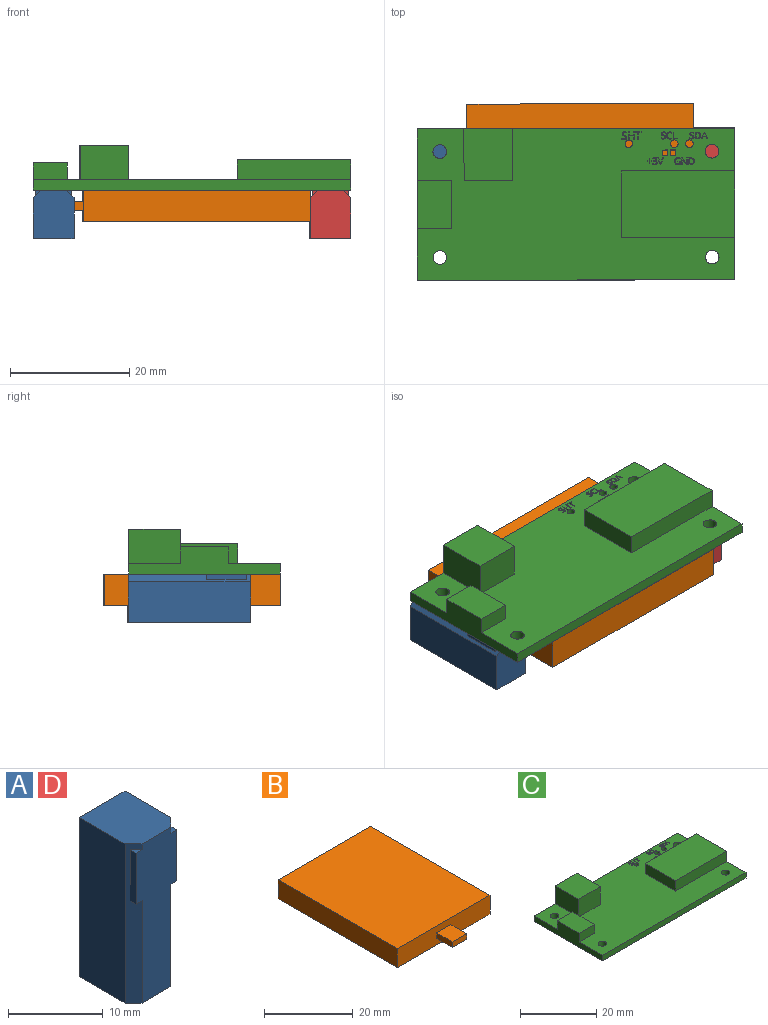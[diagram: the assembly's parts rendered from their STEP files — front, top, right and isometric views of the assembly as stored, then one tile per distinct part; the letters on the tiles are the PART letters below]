
ASSEMBLY  parts=4 mates=4
PART A: 14 faces, bbox 6.9x8.1x20.6 mm
  f0: plane 20.57x6.86mm, normal (-1,0,0), area 141.1mm2, adj f2,f3,f4,f7
  f1: plane 20.57x6.86mm, normal (1,0,0), area 141.1mm2, adj f2,f3,f4,f6
  f2: plane 20.57x6.86mm, normal (0,1,0), area 141.1mm2, adj f0,f1,f3,f4
  f3: plane 8.13x6.86mm, normal (0,0,1), area 54.1mm2, adj f0,f1,f2,f5,f6,f7
  f4: plane 8.13x6.86mm, normal (0,0,-1), area 54.1mm2, adj f0,f1,f2,f5,f6,f7
  f5: plane 20.57x6.1mm, normal (0,-1,0), area 100.6mm2, adj f3,f4,f6,f7,f8,f9,f10,f11
  f6: plane 20.57x1.27mm, normal (0.71,-0.71,0), area 28.6mm2, adj f1,f3,f4,f5,f11,f12,f13
  f7: plane 20.57x1.27mm, normal (-0.71,-0.71,0), area 28.6mm2, adj f0,f3,f4,f5,f8,f9,f10
  f8: plane 6.6x0.89mm, normal (-1,0,0), area 5.9mm2, adj f5,f7,f9,f10
  f9: plane 0.89x0.89mm, normal (0,0,-1), area 0.4mm2, adj f5,f7,f8
  f10: plane 0.89x0.89mm, normal (0,0,1), area 0.4mm2, adj f5,f7,f8
  f11: plane 0.89x0.89mm, normal (0,0,-1), area 0.4mm2, adj f5,f6,f12
  f12: plane 6.6x0.89mm, normal (1,0,0), area 5.9mm2, adj f5,f6,f11,f13
  f13: plane 0.89x0.89mm, normal (0,0,1), area 0.4mm2, adj f5,f6,f12
PART B: 11 faces, bbox 29.6x43.2x5.2 mm
  f0: plane 29.57x5.23mm, normal (0,-1,0), area 147.7mm2, adj f1,f2,f4,f5,f6,f7,f8,f9
  f1: plane 38.1x5.23mm, normal (-1,0,0), area 199.4mm2, adj f0,f3,f4,f5
  f2: plane 38.1x5.23mm, normal (1,0,0), area 199.4mm2, adj f0,f3,f4,f5
  f3: plane 29.57x5.23mm, normal (0,1,0), area 154.7mm2, adj f1,f2,f4,f5
  f4: plane 38.1x29.57mm, normal (0,0,1), area 1126.4mm2, adj f0,f1,f2,f3
  f5: plane 38.1x29.57mm, normal (0,0,-1), area 1126.4mm2, adj f0,f1,f2,f3
  f6: plane 5.08x1.52mm, normal (-1,0,0), area 7.7mm2, adj f0,f7,f9,f10
  f7: plane 5.08x4.57mm, normal (0,0,-1), area 23.2mm2, adj f0,f6,f8,f10
  f8: plane 5.08x1.52mm, normal (1,0,0), area 7.7mm2, adj f0,f7,f9,f10
  f9: plane 5.08x4.57mm, normal (0,0,1), area 23.2mm2, adj f0,f6,f8,f10
  f10: plane 4.57x1.52mm, normal (0,-1,0), area 7mm2, adj f6,f7,f8,f9
PART C: 292 faces, bbox 53.3x25.4x7.5 mm
  f0: plane 53.34x25.4mm, normal (0,0,1), area 997.2mm2, adj f1,f2,f3,f4,f5,f6,f7,f8
  f1: plane 25.4x4.57mm, normal (-1,0,0), area 67.9mm2, adj f0,f2,f19,f20,f29,f31,f32
  f2: plane 53.34x1.78mm, normal (0,-1,0), area 94.8mm2, adj f0,f1,f3,f20
  f3: plane 25.4x5.08mm, normal (1,0,0), area 82.1mm2, adj f0,f2,f19,f20,f21,f22,f24
  f4: plane 1.78x0.95mm, normal (0,-1,0), area 1.7mm2, adj f0,f5,f10,f20
  f5: plane 1.78x0.96mm, normal (-1,0,0), area 1.7mm2, adj f0,f4,f6,f20
  f6: plane 1.78x0.95mm, normal (0,1,0), area 1.7mm2, adj f0,f5,f10,f20
  f7: plane 1.78x0.88mm, normal (0,-1,0), area 1.6mm2, adj f0,f8,f11,f20
  f8: plane 1.78x0.98mm, normal (-1,0,0), area 1.7mm2, adj f0,f7,f9,f20
  f9: plane 1.78x0.88mm, normal (0,1,0), area 1.6mm2, adj f0,f8,f11,f20
  f10: plane 1.78x0.96mm, normal (1,0,0), area 1.7mm2, adj f0,f4,f6,f20
  f11: plane 1.78x0.98mm, normal (1,0,0), area 1.7mm2, adj f0,f7,f9,f20
  f12: cylinder r=1.14mm len=2.29mm, axis (0,0,-1), area 12.8mm2, adj f0,f20
  f13: cylinder r=1.14mm len=2.29mm, axis (0,0,-1), area 12.8mm2, adj f0,f20
  f14: cylinder r=1.14mm len=2.29mm, axis (0,0,-1), area 12.8mm2, adj f0,f20
  f15: cylinder r=1.14mm len=2.29mm, axis (0,0,-1), area 12.8mm2, adj f0,f20
  f16: cylinder r=0.64mm len=1.78mm, axis (0,0,-1), area 7.1mm2, adj f0,f20
  f17: cylinder r=0.64mm len=1.78mm, axis (0,0,-1), area 7.1mm2, adj f0,f20
  f18: cylinder r=0.64mm len=1.78mm, axis (0,0,-1), area 7.1mm2, adj f0,f20
  f19: plane 53.34x7.49mm, normal (0,1,0), area 141.3mm2, adj f0,f1,f3,f20,f25,f26,f28
  f20: plane 53.34x25.4mm, normal (0,0,-1), area 1332.9mm2, adj f1,f2,f3,f4,f5,f6,f7,f8
  f21: plane 19.05x3.3mm, normal (0,-1,0), area 62.9mm2, adj f0,f3,f23,f24
  f22: plane 19.05x3.3mm, normal (0,1,0), area 62.9mm2, adj f0,f3,f23,f24
  f23: plane 11.18x3.3mm, normal (-1,0,0), area 36.9mm2, adj f0,f21,f22,f24
  f24: plane 19.05x11.18mm, normal (0,0,1), area 212.9mm2, adj f3,f21,f22,f23
  f25: plane 8.64x5.72mm, normal (1,0,0), area 49.4mm2, adj f0,f19,f27,f28
  f26: plane 8.64x5.72mm, normal (-1,0,0), area 49.4mm2, adj f0,f19,f27,f28
  f27: plane 8.13x5.72mm, normal (0,-1,0), area 46.5mm2, adj f0,f25,f26,f28
  f28: plane 8.64x8.13mm, normal (0,0,1), area 70.2mm2, adj f19,f25,f26,f27
  f29: plane 5.72x2.79mm, normal (0,-1,0), area 16mm2, adj f0,f1,f30,f32
  f30: plane 8.13x2.79mm, normal (1,0,0), area 22.7mm2, adj f0,f29,f31,f32
  f31: plane 5.72x2.79mm, normal (0,1,0), area 16mm2, adj f0,f1,f30,f32
  f32: plane 8.13x5.72mm, normal (0,0,1), area 46.5mm2, adj f1,f29,f30,f31
  f33: extruded ~0.19x0.13mm, area 0mm2, adj f0,f34,f57,f58
  f34: extruded ~0.25x0.14mm, area 0mm2, adj f0,f33,f35,f58
  f35: extruded ~0.16x0.13mm, area 0mm2, adj f0,f34,f36,f58
  f36: extruded ~0.13x0.07mm, area 0mm2, adj f0,f35,f37,f58
  f37: extruded ~0.13x0.1mm, area 0mm2, adj f0,f36,f38,f58
  f38: extruded ~0.13x0.13mm, area 0mm2, adj f0,f37,f39,f58
  f39: extruded ~0.17x0.13mm, area 0mm2, adj f0,f38,f40,f58
  f40: extruded ~0.28x0.13mm, area 0mm2, adj f0,f39,f41,f58
  f41: plane 0.13x0.12mm, normal (-0.94,0.34,0), area 0mm2, adj f0,f40,f42,f58
  f42: extruded ~0.31x0.13mm, area 0mm2, adj f0,f41,f43,f58
  f43: extruded ~0.26x0.13mm, area 0mm2, adj f0,f42,f44,f58
  f44: extruded ~0.21x0.13mm, area 0mm2, adj f0,f43,f45,f58
  f45: extruded ~0.2x0.13mm, area 0mm2, adj f0,f44,f46,f58
  f46: extruded ~0.23x0.14mm, area 0mm2, adj f0,f45,f47,f58
  f47: extruded ~0.17x0.13mm, area 0mm2, adj f0,f46,f48,f58
  f48: extruded ~0.13x0.08mm, area 0mm2, adj f0,f47,f49,f58
  f49: extruded ~0.13x0.1mm, area 0mm2, adj f0,f48,f50,f58
  f50: extruded ~0.14x0.13mm, area 0mm2, adj f0,f49,f51,f58
  f51: extruded ~0.2x0.13mm, area 0mm2, adj f0,f50,f52,f58
  f52: extruded ~0.16x0.13mm, area 0mm2, adj f0,f51,f53,f58
  f53: extruded ~0.15x0.13mm, area 0mm2, adj f0,f52,f54,f58
  f54: plane 0.13x0.13mm, normal (1,0,0), area 0mm2, adj f0,f53,f55,f58
  f55: extruded ~0.31x0.13mm, area 0mm2, adj f0,f54,f56,f58
  f56: extruded ~0.3x0.13mm, area 0mm2, adj f0,f55,f57,f58
  f57: extruded ~0.24x0.13mm, area 0mm2, adj f0,f33,f56,f58
  f58: plane 1.18x0.72mm, normal (0,0,1), area 0.3mm2, adj f33,f34,f35,f36,f37,f38,f39,f40
  f59: extruded ~0.22x0.13mm, area 0mm2, adj f0,f60,f83,f84
  f60: extruded ~0.28x0.16mm, area 0mm2, adj f0,f59,f61,f84
  f61: extruded ~0.18x0.13mm, area 0mm2, adj f0,f60,f62,f84
  f62: extruded ~0.13x0.08mm, area 0mm2, adj f0,f61,f63,f84
  f63: extruded ~0.13x0.11mm, area 0mm2, adj f0,f62,f64,f84
  f64: extruded ~0.14x0.13mm, area 0mm2, adj f0,f63,f65,f84
  f65: extruded ~0.19x0.13mm, area 0mm2, adj f0,f64,f66,f84
  f66: extruded ~0.31x0.13mm, area 0mm2, adj f0,f65,f67,f84
  f67: plane 0.13x0.13mm, normal (-0.94,0.34,0), area 0mm2, adj f0,f66,f68,f84
  f68: extruded ~0.36x0.13mm, area 0mm2, adj f0,f67,f69,f84
  f69: extruded ~0.3x0.13mm, area 0mm2, adj f0,f68,f70,f84
  f70: extruded ~0.24x0.13mm, area 0mm2, adj f0,f69,f71,f84
  f71: extruded ~0.23x0.13mm, area 0mm2, adj f0,f70,f72,f84
  f72: extruded ~0.26x0.15mm, area 0mm2, adj f0,f71,f73,f84
  f73: extruded ~0.19x0.13mm, area 0mm2, adj f0,f72,f74,f84
  f74: extruded ~0.13x0.09mm, area 0mm2, adj f0,f73,f75,f84
  f75: extruded ~0.13x0.11mm, area 0mm2, adj f0,f74,f76,f84
  f76: extruded ~0.16x0.13mm, area 0mm2, adj f0,f75,f77,f84
  f77: extruded ~0.23x0.13mm, area 0mm2, adj f0,f76,f78,f84
  f78: extruded ~0.19x0.13mm, area 0mm2, adj f0,f77,f79,f84
  f79: extruded ~0.17x0.13mm, area 0mm2, adj f0,f78,f80,f84
  f80: plane 0.15x0.13mm, normal (1,0,0), area 0mm2, adj f0,f79,f81,f84
  f81: extruded ~0.35x0.13mm, area 0mm2, adj f0,f80,f82,f84
  f82: extruded ~0.34x0.13mm, area 0mm2, adj f0,f81,f83,f84
  f83: extruded ~0.27x0.13mm, area 0mm2, adj f0,f59,f82,f84
  f84: plane 1.33x0.81mm, normal (0,0,1), area 0.4mm2, adj f59,f60,f61,f62,f63,f64,f65,f66
  f85: plane 1.29x0.13mm, normal (-1,0,0), area 0.2mm2, adj f0,f86,f96,f97
  f86: plane 0.15x0.13mm, normal (0,-1,0), area 0mm2, adj f0,f85,f87,f97
  f87: plane 0.55x0.13mm, normal (1,0,0), area 0.1mm2, adj f0,f86,f88,f97
  f88: plane 0.68x0.13mm, normal (0,-1,0), area 0.1mm2, adj f0,f87,f89,f97
  f89: plane 0.55x0.13mm, normal (-1,0,0), area 0.1mm2, adj f0,f88,f90,f97
  f90: plane 0.15x0.13mm, normal (0,-1,0), area 0mm2, adj f0,f89,f91,f97
  f91: plane 1.29x0.13mm, normal (1,0,0), area 0.2mm2, adj f0,f90,f92,f97
  f92: plane 0.15x0.13mm, normal (0,1,0), area 0mm2, adj f0,f91,f93,f97
  f93: plane 0.61x0.13mm, normal (-1,0,0), area 0.1mm2, adj f0,f92,f94,f97
  f94: plane 0.68x0.13mm, normal (0,1,0), area 0.1mm2, adj f0,f93,f95,f97
  f95: plane 0.61x0.13mm, normal (1,0,0), area 0.1mm2, adj f0,f94,f96,f97
  f96: plane 0.15x0.13mm, normal (0,1,0), area 0mm2, adj f0,f85,f95,f97
  f97: plane 1.29x0.98mm, normal (0,0,1), area 0.5mm2, adj f85,f86,f87,f88,f89,f90,f91,f92
  f98: plane 1.16x0.13mm, normal (-1,0,0), area 0.1mm2, adj f0,f99,f105,f106
  f99: plane 0.41x0.13mm, normal (0,1,0), area 0.1mm2, adj f0,f98,f100,f106
  f100: plane 0.13x0.13mm, normal (-1,0,0), area 0mm2, adj f0,f99,f101,f106
  f101: plane 0.97x0.13mm, normal (0,-1,0), area 0.1mm2, adj f0,f100,f102,f106
  f102: plane 0.13x0.13mm, normal (1,0,0), area 0mm2, adj f0,f101,f103,f106
  f103: plane 0.41x0.13mm, normal (0,1,0), area 0.1mm2, adj f0,f102,f104,f106
  f104: plane 1.16x0.13mm, normal (1,0,0), area 0.1mm2, adj f0,f103,f105,f106
  f105: plane 0.15x0.13mm, normal (0,1,0), area 0mm2, adj f0,f98,f104,f106
  f106: plane 1.29x0.97mm, normal (0,0,1), area 0.3mm2, adj f98,f99,f100,f101,f102,f103,f104,f105
  f107: extruded ~0.41x0.15mm, area 0.1mm2, adj f0,f108,f120,f121
  f108: extruded ~0.41x0.15mm, area 0.1mm2, adj f0,f107,f109,f121
  f109: plane 0.35x0.13mm, normal (0,-1,0), area 0mm2, adj f0,f108,f110,f121
  f110: plane 1.14x0.13mm, normal (1,0,0), area 0.1mm2, adj f0,f109,f111,f121
  f111: plane 0.32x0.13mm, normal (0,1,0), area 0mm2, adj f0,f110,f112,f121
  f112: extruded ~0.44x0.15mm, area 0.1mm2, adj f0,f111,f120,f121
  f113: extruded ~0.35x0.13mm, area 0mm2, adj f114,f119,f121,f122
  f114: extruded ~0.36x0.13mm, area 0mm2, adj f113,f115,f121,f122
  f115: plane 0.16x0.13mm, normal (0,-1,0), area 0mm2, adj f114,f116,f121,f122
  f116: plane 0.91x0.13mm, normal (-1,0,0), area 0.1mm2, adj f115,f117,f121,f122
  f117: plane 0.19x0.13mm, normal (0,1,0), area 0mm2, adj f116,f118,f121,f122
  f118: extruded ~0.33x0.13mm, area 0mm2, adj f117,f119,f121,f122
  f119: extruded ~0.34x0.13mm, area 0mm2, adj f113,f118,f121,f122
  f120: extruded ~0.43x0.15mm, area 0.1mm2, adj f0,f107,f112,f121
  f121: plane 1.14x0.91mm, normal (0,0,1), area 0.4mm2, adj f107,f108,f109,f110,f111,f112,f113,f114
  f122: plane 0.91x0.64mm, normal (0,0,1), area 0.5mm2, adj f113,f114,f115,f116,f117,f118,f119
  f123: plane 0.14x0.13mm, normal (0,1,0), area 0mm2, adj f0,f124,f135,f136
  f124: plane 1.15x0.45mm, normal (-0.93,-0.36,0), area 0.2mm2, adj f0,f123,f125,f136
  f125: plane 0.13x0.11mm, normal (0,-1,0), area 0mm2, adj f0,f124,f126,f136
  f126: plane 1.15x0.45mm, normal (0.93,-0.37,0), area 0.2mm2, adj f0,f125,f127,f136
  f127: plane 0.13x0.13mm, normal (0,1,0), area 0mm2, adj f0,f126,f128,f136
  f128: plane 0.36x0.14mm, normal (-0.93,0.36,0), area 0mm2, adj f0,f127,f129,f136
  f129: plane 0.46x0.13mm, normal (0,1,0), area 0.1mm2, adj f0,f128,f135,f136
  f130: plane 0.37x0.13mm, normal (0,-1,0), area 0mm2, adj f131,f134,f136,f137
  f131: plane 0.35x0.13mm, normal (-0.94,0.35,0), area 0mm2, adj f130,f132,f136,f137
  f132: extruded ~0.17x0.13mm, area 0mm2, adj f131,f133,f136,f137
  f133: extruded ~0.17x0.13mm, area 0mm2, adj f132,f134,f136,f137
  f134: plane 0.35x0.13mm, normal (0.94,0.35,0), area 0mm2, adj f130,f133,f136,f137
  f135: plane 0.36x0.14mm, normal (0.93,0.36,0), area 0mm2, adj f0,f123,f129,f136
  f136: plane 1.15x1.01mm, normal (0,0,1), area 0.3mm2, adj f123,f124,f125,f126,f127,f128,f129,f130
  f137: plane 0.52x0.37mm, normal (0,0,1), area 0.1mm2, adj f130,f131,f132,f133,f134
  f138: extruded ~0.41x0.15mm, area 0.1mm2, adj f0,f139,f151,f152
  f139: extruded ~0.41x0.15mm, area 0.1mm2, adj f0,f138,f140,f152
  f140: plane 0.34x0.13mm, normal (0,-1,0), area 0mm2, adj f0,f139,f141,f152
  f141: plane 1.12x0.13mm, normal (1,0,0), area 0.1mm2, adj f0,f140,f142,f152
  f142: plane 0.31x0.13mm, normal (0,1,0), area 0mm2, adj f0,f141,f143,f152
  f143: extruded ~0.43x0.15mm, area 0.1mm2, adj f0,f142,f151,f152
  f144: extruded ~0.34x0.13mm, area 0mm2, adj f145,f150,f152,f153
  f145: extruded ~0.35x0.13mm, area 0mm2, adj f144,f146,f152,f153
  f146: plane 0.16x0.13mm, normal (0,-1,0), area 0mm2, adj f145,f147,f152,f153
  f147: plane 0.9x0.13mm, normal (-1,0,0), area 0.1mm2, adj f146,f148,f152,f153
  f148: plane 0.19x0.13mm, normal (0,1,0), area 0mm2, adj f147,f149,f152,f153
  f149: extruded ~0.33x0.13mm, area 0mm2, adj f148,f150,f152,f153
  f150: extruded ~0.33x0.13mm, area 0mm2, adj f144,f149,f152,f153
  f151: extruded ~0.43x0.15mm, area 0.1mm2, adj f0,f138,f143,f152
  f152: plane 1.12x0.9mm, normal (0,0,1), area 0.4mm2, adj f138,f139,f140,f141,f142,f143,f144,f145
  f153: plane 0.9x0.63mm, normal (0,0,1), area 0.5mm2, adj f144,f145,f146,f147,f148,f149,f150
  f154: extruded ~0.19x0.13mm, area 0mm2, adj f0,f155,f178,f179
  f155: extruded ~0.25x0.14mm, area 0mm2, adj f0,f154,f156,f179
  f156: extruded ~0.16x0.13mm, area 0mm2, adj f0,f155,f157,f179
  f157: extruded ~0.13x0.08mm, area 0mm2, adj f0,f156,f158,f179
  f158: extruded ~0.13x0.1mm, area 0mm2, adj f0,f157,f159,f179
  f159: extruded ~0.13x0.13mm, area 0mm2, adj f0,f158,f160,f179
  f160: extruded ~0.17x0.13mm, area 0mm2, adj f0,f159,f161,f179
  f161: extruded ~0.28x0.13mm, area 0mm2, adj f0,f160,f162,f179
  f162: plane 0.13x0.12mm, normal (-0.94,0.34,0), area 0mm2, adj f0,f161,f163,f179
  f163: extruded ~0.32x0.13mm, area 0mm2, adj f0,f162,f164,f179
  f164: extruded ~0.27x0.13mm, area 0mm2, adj f0,f163,f165,f179
  f165: extruded ~0.21x0.13mm, area 0mm2, adj f0,f164,f166,f179
  f166: extruded ~0.21x0.13mm, area 0mm2, adj f0,f165,f167,f179
  f167: extruded ~0.23x0.14mm, area 0mm2, adj f0,f166,f168,f179
  f168: extruded ~0.17x0.13mm, area 0mm2, adj f0,f167,f169,f179
  f169: extruded ~0.13x0.08mm, area 0mm2, adj f0,f168,f170,f179
  f170: extruded ~0.13x0.1mm, area 0mm2, adj f0,f169,f171,f179
  f171: extruded ~0.14x0.13mm, area 0mm2, adj f0,f170,f172,f179
  f172: extruded ~0.2x0.13mm, area 0mm2, adj f0,f171,f173,f179
  f173: extruded ~0.17x0.13mm, area 0mm2, adj f0,f172,f174,f179
  f174: extruded ~0.16x0.13mm, area 0mm2, adj f0,f173,f175,f179
  f175: plane 0.13x0.13mm, normal (1,0,0), area 0mm2, adj f0,f174,f176,f179
  f176: extruded ~0.32x0.13mm, area 0mm2, adj f0,f175,f177,f179
  f177: extruded ~0.3x0.13mm, area 0mm2, adj f0,f176,f178,f179
  f178: extruded ~0.24x0.13mm, area 0mm2, adj f0,f154,f177,f179
  f179: plane 1.2x0.73mm, normal (0,0,1), area 0.3mm2, adj f154,f155,f156,f157,f158,f159,f160,f161
  f180: extruded ~0.26x0.13mm, area 0mm2, adj f0,f181,f194,f195
  f181: plane 0.13x0.12mm, normal (-0.9,0.44,0), area 0mm2, adj f0,f180,f182,f195
  f182: extruded ~0.32x0.13mm, area 0mm2, adj f0,f181,f183,f195
  f183: extruded ~0.3x0.13mm, area 0mm2, adj f0,f182,f184,f195
  f184: extruded ~0.21x0.19mm, area 0mm2, adj f0,f183,f185,f195
  f185: extruded ~0.32x0.13mm, area 0mm2, adj f0,f184,f186,f195
  f186: extruded ~0.44x0.14mm, area 0.1mm2, adj f0,f185,f187,f195
  f187: extruded ~0.4x0.16mm, area 0.1mm2, adj f0,f186,f188,f195
  f188: extruded ~0.3x0.13mm, area 0mm2, adj f0,f187,f189,f195
  f189: plane 0.13x0.12mm, normal (-1,0,0), area 0mm2, adj f0,f188,f190,f195
  f190: extruded ~0.28x0.13mm, area 0mm2, adj f0,f189,f191,f195
  f191: extruded ~0.31x0.13mm, area 0mm2, adj f0,f190,f192,f195
  f192: extruded ~0.35x0.13mm, area 0mm2, adj f0,f191,f193,f195
  f193: extruded ~0.35x0.13mm, area 0mm2, adj f0,f192,f194,f195
  f194: extruded ~0.3x0.13mm, area 0mm2, adj f0,f180,f193,f195
  f195: plane 1.2x0.88mm, normal (0,0,1), area 0.3mm2, adj f180,f181,f182,f183,f184,f185,f186,f187
  f196: plane 0.65x0.13mm, normal (0,1,0), area 0.1mm2, adj f0,f197,f201,f202
  f197: plane 0.13x0.12mm, normal (-1,0,0), area 0mm2, adj f0,f196,f198,f202
  f198: plane 0.51x0.13mm, normal (0,-1,0), area 0.1mm2, adj f0,f197,f199,f202
  f199: plane 1.04x0.13mm, normal (-1,0,0), area 0.1mm2, adj f0,f198,f200,f202
  f200: plane 0.14x0.13mm, normal (0,-1,0), area 0mm2, adj f0,f199,f201,f202
  f201: plane 1.16x0.13mm, normal (1,0,0), area 0.1mm2, adj f0,f196,f200,f202
  f202: plane 1.16x0.65mm, normal (0,0,1), area 0.2mm2, adj f196,f197,f198,f199,f200,f201
  f203: plane 0.13x0.12mm, normal (1,0,0), area 0mm2, adj f0,f204,f222,f223
  f204: plane 0.25x0.13mm, normal (0,1,0), area 0mm2, adj f0,f203,f205,f223
  f205: plane 0.35x0.13mm, normal (1,0,0), area 0mm2, adj f0,f204,f206,f223
  f206: extruded ~0.23x0.13mm, area 0mm2, adj f0,f205,f207,f223
  f207: extruded ~0.33x0.13mm, area 0mm2, adj f0,f206,f208,f223
  f208: extruded ~0.35x0.13mm, area 0mm2, adj f0,f207,f209,f223
  f209: extruded ~0.34x0.13mm, area 0mm2, adj f0,f208,f210,f223
  f210: extruded ~0.32x0.13mm, area 0mm2, adj f0,f209,f211,f223
  f211: extruded ~0.29x0.13mm, area 0mm2, adj f0,f210,f212,f223
  f212: plane 0.13x0.12mm, normal (-0.92,0.4,0), area 0mm2, adj f0,f211,f213,f223
  f213: extruded ~0.34x0.13mm, area 0mm2, adj f0,f212,f214,f223
  f214: extruded ~0.31x0.13mm, area 0mm2, adj f0,f213,f215,f223
  f215: extruded ~0.2x0.2mm, area 0mm2, adj f0,f214,f216,f223
  f216: extruded ~0.31x0.13mm, area 0mm2, adj f0,f215,f217,f223
  f217: extruded ~0.43x0.14mm, area 0.1mm2, adj f0,f216,f218,f223
  f218: extruded ~0.4x0.15mm, area 0.1mm2, adj f0,f217,f219,f223
  f219: extruded ~0.21x0.13mm, area 0mm2, adj f0,f218,f220,f223
  f220: extruded ~0.18x0.13mm, area 0mm2, adj f0,f219,f221,f223
  f221: plane 0.55x0.13mm, normal (-1,0,0), area 0.1mm2, adj f0,f220,f222,f223
  f222: plane 0.38x0.13mm, normal (0,-1,0), area 0mm2, adj f0,f203,f221,f223
  f223: plane 1.16x0.93mm, normal (0,0,1), area 0.4mm2, adj f203,f204,f205,f206,f207,f208,f209,f210
  f224: plane 0.75x0.27mm, normal (0.94,-0.33,0), area 0.1mm2, adj f0,f225,f232,f233
  f225: extruded ~0.26x0.13mm, area 0mm2, adj f0,f224,f226,f233
  f226: extruded ~0.25x0.13mm, area 0mm2, adj f0,f225,f227,f233
  f227: plane 0.75x0.27mm, normal (-0.94,-0.33,0), area 0.1mm2, adj f0,f226,f228,f233
  f228: plane 0.14x0.13mm, normal (0,-1,0), area 0mm2, adj f0,f227,f229,f233
  f229: plane 1.16x0.42mm, normal (0.94,0.34,0), area 0.2mm2, adj f0,f228,f230,f233
  f230: plane 0.13x0.13mm, normal (0,1,0), area 0mm2, adj f0,f229,f231,f233
  f231: plane 1.16x0.42mm, normal (-0.94,0.34,0), area 0.2mm2, adj f0,f230,f232,f233
  f232: plane 0.15x0.13mm, normal (0,-1,0), area 0mm2, adj f0,f224,f231,f233
  f233: plane 1.16x0.97mm, normal (0,0,1), area 0.3mm2, adj f224,f225,f226,f227,f228,f229,f230,f231
  f234: extruded ~0.21x0.13mm, area 0mm2, adj f0,f235,f261,f262
  f235: extruded ~0.26x0.13mm, area 0mm2, adj f0,f234,f236,f262
  f236: extruded ~0.2x0.13mm, area 0mm2, adj f0,f235,f237,f262
  f237: extruded ~0.17x0.13mm, area 0mm2, adj f0,f236,f238,f262
  f238: plane 0.13x0.09mm, normal (0.8,0.6,0), area 0mm2, adj f0,f237,f239,f262
  f239: extruded ~0.15x0.13mm, area 0mm2, adj f0,f238,f240,f262
  f240: extruded ~0.14x0.13mm, area 0mm2, adj f0,f239,f241,f262
  f241: extruded ~0.16x0.13mm, area 0mm2, adj f0,f240,f242,f262
  f242: extruded ~0.13x0.13mm, area 0mm2, adj f0,f241,f243,f262
  f243: extruded ~0.17x0.13mm, area 0mm2, adj f0,f242,f244,f262
  f244: extruded ~0.22x0.13mm, area 0mm2, adj f0,f243,f245,f262
  f245: plane 0.13x0.12mm, normal (0,-1,0), area 0mm2, adj f0,f244,f246,f262
  f246: plane 0.13x0.11mm, normal (1,0,0), area 0mm2, adj f0,f245,f247,f262
  f247: plane 0.13x0.11mm, normal (0,1,0), area 0mm2, adj f0,f246,f248,f262
  f248: extruded ~0.33x0.21mm, area 0.1mm2, adj f0,f247,f249,f262
  f249: extruded ~0.3x0.24mm, area 0.1mm2, adj f0,f248,f250,f262
  f250: extruded ~0.16x0.13mm, area 0mm2, adj f0,f249,f251,f262
  f251: extruded ~0.16x0.13mm, area 0mm2, adj f0,f250,f252,f262
  f252: plane 0.13x0.13mm, normal (1,0,0), area 0mm2, adj f0,f251,f253,f262
  f253: extruded ~0.15x0.13mm, area 0mm2, adj f0,f252,f254,f262
  f254: extruded ~0.17x0.13mm, area 0mm2, adj f0,f253,f255,f262
  f255: extruded ~0.33x0.13mm, area 0mm2, adj f0,f254,f256,f262
  f256: extruded ~0.26x0.13mm, area 0mm2, adj f0,f255,f257,f262
  f257: extruded ~0.19x0.13mm, area 0mm2, adj f0,f256,f258,f262
  f258: extruded ~0.21x0.13mm, area 0mm2, adj f0,f257,f259,f262
  f259: plane 0.13x0.01mm, normal (-1,0,0), area 0mm2, adj f0,f258,f260,f262
  f260: extruded ~0.18x0.13mm, area 0mm2, adj f0,f259,f261,f262
  f261: extruded ~0.18x0.13mm, area 0mm2, adj f0,f234,f260,f262
  f262: plane 1.2x0.76mm, normal (0,0,1), area 0.3mm2, adj f234,f235,f236,f237,f238,f239,f240,f241
  f263: plane 0.34x0.13mm, normal (-1,0,0), area 0mm2, adj f0,f264,f274,f275
  f264: plane 0.13x0.11mm, normal (0,-1,0), area 0mm2, adj f0,f263,f265,f275
  f265: plane 0.34x0.13mm, normal (1,0,0), area 0mm2, adj f0,f264,f266,f275
  f266: plane 0.33x0.13mm, normal (0,-1,0), area 0mm2, adj f0,f265,f267,f275
  f267: plane 0.13x0.11mm, normal (1,0,0), area 0mm2, adj f0,f266,f268,f275
  f268: plane 0.33x0.13mm, normal (0,1,0), area 0mm2, adj f0,f267,f269,f275
  f269: plane 0.34x0.13mm, normal (1,0,0), area 0mm2, adj f0,f268,f270,f275
  f270: plane 0.13x0.11mm, normal (0,1,0), area 0mm2, adj f0,f269,f271,f275
  f271: plane 0.34x0.13mm, normal (-1,0,0), area 0mm2, adj f0,f270,f272,f275
  f272: plane 0.33x0.13mm, normal (0,1,0), area 0mm2, adj f0,f271,f273,f275
  f273: plane 0.13x0.11mm, normal (-1,0,0), area 0mm2, adj f0,f272,f274,f275
  f274: plane 0.33x0.13mm, normal (0,-1,0), area 0mm2, adj f0,f263,f273,f275
  f275: plane 0.79x0.77mm, normal (0,0,1), area 0.2mm2, adj f263,f264,f265,f266,f267,f268,f269,f270
  f276: plane 1.12x0.13mm, normal (-1,0,0), area 0.1mm2, adj f0,f277,f290,f291
  f277: plane 0.13x0.12mm, normal (0,-1,0), area 0mm2, adj f0,f276,f278,f291
  f278: plane 0.64x0.13mm, normal (1,0,0), area 0.1mm2, adj f0,f277,f279,f291
  f279: extruded ~0.16x0.13mm, area 0mm2, adj f0,f278,f280,f291
  f280: extruded ~0.13x0.13mm, area 0mm2, adj f0,f279,f281,f291
  f281: plane 0.13x0.01mm, normal (0,-1,0), area 0mm2, adj f0,f280,f282,f291
  f282: plane 0.94x0.61mm, normal (-0.84,-0.55,0), area 0.1mm2, adj f0,f281,f283,f291
  f283: plane 0.15x0.13mm, normal (0,-1,0), area 0mm2, adj f0,f282,f284,f291
  f284: plane 1.12x0.13mm, normal (1,0,0), area 0.1mm2, adj f0,f283,f285,f291
  f285: plane 0.13x0.12mm, normal (0,1,0), area 0mm2, adj f0,f284,f286,f291
  f286: plane 0.64x0.13mm, normal (-1,0,0), area 0.1mm2, adj f0,f285,f287,f291
  f287: extruded ~0.3x0.13mm, area 0mm2, adj f0,f286,f288,f291
  f288: plane 0.13x0.01mm, normal (0,1,0), area 0mm2, adj f0,f287,f289,f291
  f289: plane 0.94x0.61mm, normal (0.84,0.55,0), area 0.1mm2, adj f0,f288,f290,f291
  f290: plane 0.15x0.13mm, normal (0,1,0), area 0mm2, adj f0,f276,f289,f291
  f291: plane 1.12x0.88mm, normal (0,0,1), area 0.4mm2, adj f276,f277,f278,f279,f280,f281,f282,f283
PART D: same geometry as A
PLACE A rot(axis=(0,0.71,-0.71),179.9deg) t=(-10.21,17.8,-29.12)mm
PLACE B rot(axis=(0.71,0.71,0),180deg) t=(13.81,7.08,-24.42)mm
PLACE C rot(axis=(0,0,1),0.1deg) t=(13.05,5,-24.42)mm
PLACE D rot(axis=(0,0.71,-0.71),179.9deg) t=(36.28,17.86,-29.12)mm
MATE parallel C.f2 <-> B.f1  axis (0,-1,0) through (13.07,-7.7,-23.53)mm
MATE parallel B.f3 <-> D.f1  axis (1,0,0) through (32.86,7.11,-27.04)mm
MATE parallel C.f1 <-> A.f1  axis (-1,0,0) through (-13.62,4.97,-22.77)mm
MATE parallel D.f0 <-> C.f3  axis (1,0,0) through (39.72,7.57,-29.12)mm
